# Revit family: Two Handle Lavatory Faucet_TOTO_TLG04201
name_source: partatom
category: Plumbing Fixtures
revit_build: Autodesk Revit 2018 (Build: 20190510_1515(x64)
units: mm (PartAtom-declared; Revit-internal decimal feet)

## family parameters
Always vertical = Yes
Cut with Voids When Loaded = No
OmniClass Number = 23.45.00.00
OmniClass Title = Sanitary, Laundry, and Cleaning Equipment
Part Type = Normal
Room Calculation Point = No
Round Connector Dimension = Use Diameter
Shared = No
Work Plane-Based = No

## types (1)
- Two Handle Lavatory Faucet_TOTO_TLG04201
    Description = Two Handle Lavatory Faucet/双柄双控洗面器水嘴
    Finish = faucet_material
    Height = 110 mm  [stored 0.360892 ft]
    Length = 180.5 mm
    Manufacturer = TOTO Ltd.
    Model = TLG04201
    TOTO AsiaOceania = TBG04201B
    TOTO AsiaOceania URL = http://asia.toto.com
    TOTO China = TLG04201B
    TOTO China URL = http://www.toto.com.cn
    TOTO HongKong = TLG04201B
    TOTO HongKong URL = http://hk.toto.com
    TOTO India = TLG04201B
    TOTO India URL = https://in.toto.com
    TOTO Korea = TLG04201K
    TOTO Korea URL = https://kr.toto.com
    TOTO Taiwan = TLG04201B
    TOTO Taiwan URL = https://www.twtoto.com.tw
    TOTO Thailand = TLG04201T
    TOTO Thailand URL = https://th.toto.com
    TOTO Vietnam = TLG04201B
    TOTO Vietnam URL = https://vn.toto.com
    Width = 340.1 mm

note: [stored X ft] marks values corroborated as IEEE doubles in the binary element streams (Revit-internal decimal feet)

## geometry (parser evidence)
native form markers: Blend x2, Sweep x1
no freeform markers — native parametric forms only
